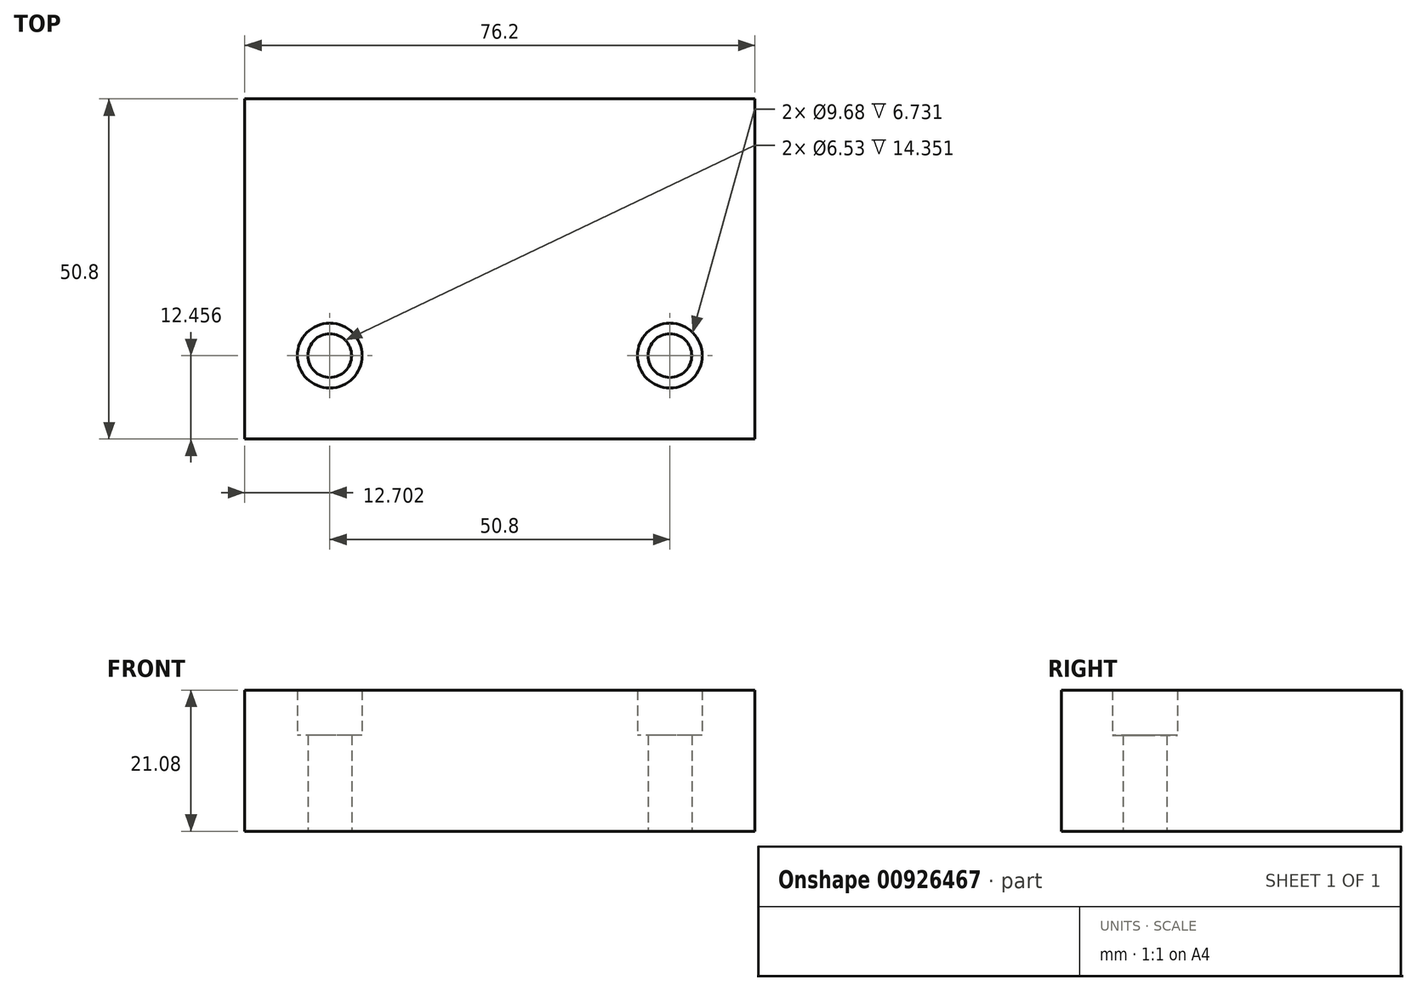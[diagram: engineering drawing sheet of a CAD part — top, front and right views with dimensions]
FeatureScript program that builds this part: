
annotation { "Feature Type Name" : "Feature", "Feature Type Description" : "" }
export const myFeature = defineFeature(function(context is Context, id is Id, definition is map)
    precondition{}
    {
        {
            var Q0;
            Q0=qCreatedBy(makeId("Top.planeOp"),FACE);
            var sketch = newSketch(context, id + "F0", { "sketchPlane" : qUnion([Q0])});
            skLineSegment(sketch, "E0.bottom", {"start": v(-38.08, 37.18) * mm, "end": v(38.12, 37.18) * mm});
            skLineSegment(sketch, "E0.top", {"start": v(-38.08, -13.62) * mm, "end": v(38.12, -13.62) * mm});
            skLineSegment(sketch, "E0.left", {"start": v(-38.08, 37.18) * mm, "end": v(-38.08, -13.62) * mm});
            skLineSegment(sketch, "E0.right", {"start": v(38.12, 37.18) * mm, "end": v(38.12, -13.62) * mm});
            skCircle(sketch, "E1", {"center": v(-25.38, -1.16) * mm, "radius": 4.84 * mm});
            skCircle(sketch, "E2", {"center": v(25.42, -1.16) * mm, "radius": 4.84 * mm});
            skCircle(sketch, "E3", {"center": v(-25.38, -1.16) * mm, "radius": 3.26 * mm});
            skCircle(sketch, "E4", {"center": v(25.42, -1.16) * mm, "radius": 3.26 * mm});
            skSolve(sketch);
        }
        {
            var Q0;
            Q0=makeQuery(id+"F0.imprint","IMPRINT",FACE,{"disambiguationData":[TD([[makeQuery(id+"F0.imprint","IMPRINT",EDGE,{"derivedFrom":sQuery(id+"F0.wireOp",EDGE,"E0.bottom")}),-1.0]])]});
            extrude(context, id + "F1", {"entities" : qUnion([Q0]), "depth" : 21.08 * mm, "offsetDistance" : 25.4 * mm});
        }
        {
            var Q0;
            Q0=makeQuery(id+"F0.imprint","IMPRINT",FACE,{"disambiguationData":[TD([[makeQuery(id+"F0.imprint","IMPRINT",EDGE,{"derivedFrom":sQuery(id+"F0.wireOp",EDGE,"E1")}),1.0]])]});
            var Q1;
            Q1=makeQuery(id+"F0.imprint","IMPRINT",FACE,{"disambiguationData":[TD([[makeQuery(id+"F0.imprint","IMPRINT",EDGE,{"derivedFrom":sQuery(id+"F0.wireOp",EDGE,"E2")}),1.0]])]});
            extrude(context, id + "F2", {"entities" : qUnion([Q0, Q1]), "operationType" : NewBodyOperationType.ADD, "depth" : 14.35 * mm, "offsetDistance" : 25.4 * mm});
        }
    });
